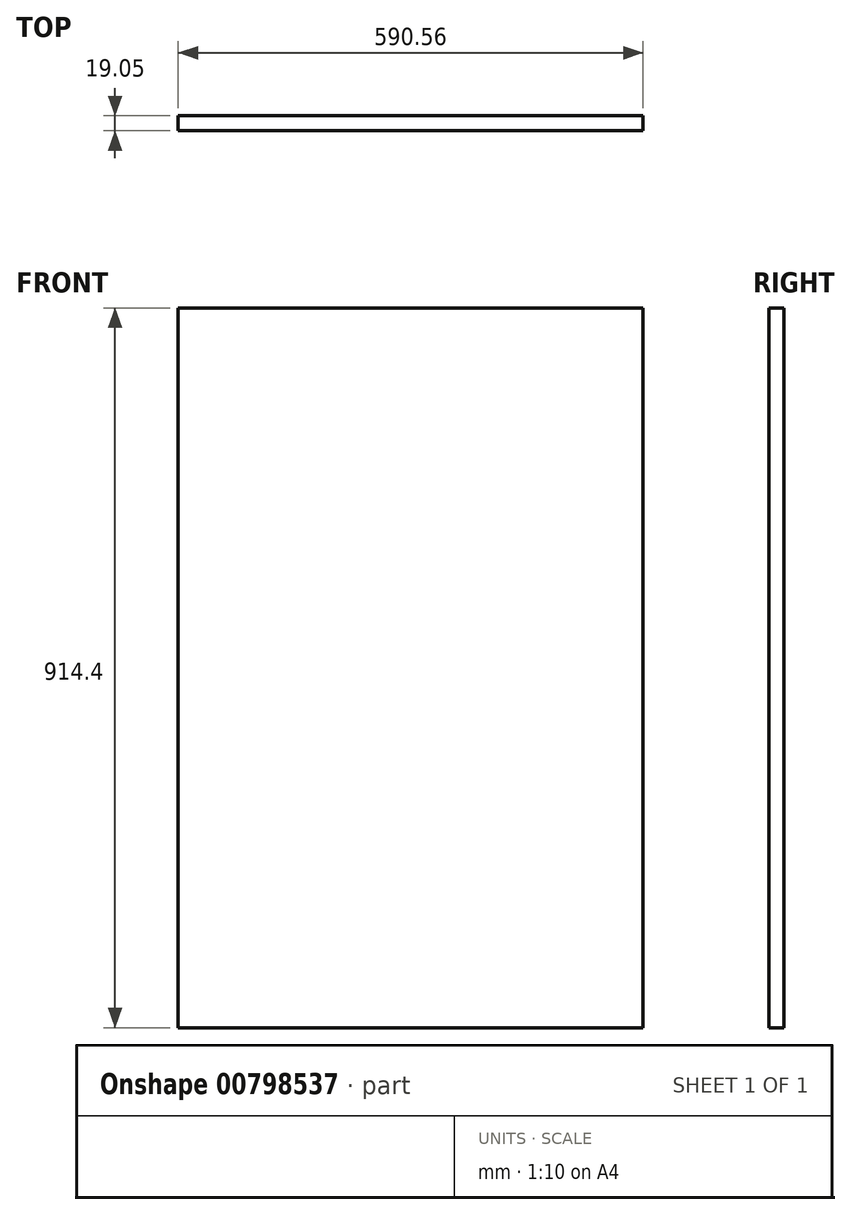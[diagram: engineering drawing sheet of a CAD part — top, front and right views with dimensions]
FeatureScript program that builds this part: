
annotation { "Feature Type Name" : "Feature", "Feature Type Description" : "" }
export const myFeature = defineFeature(function(context is Context, id is Id, definition is map)
    precondition{}
    {
        {
            var Q0;
            Q0=qCreatedBy(makeId("Front.planeOp"),FACE);
            var sketch = newSketch(context, id + "F0", { "sketchPlane" : qUnion([Q0])});
            skLineSegment(sketch, "E0.bottom", {"start": v(295.28, 457.2) * mm, "end": v(-295.28, 457.2) * mm});
            skLineSegment(sketch, "E0.top", {"start": v(295.28, -457.2) * mm, "end": v(-295.28, -457.2) * mm});
            skLineSegment(sketch, "E0.left", {"start": v(295.28, 457.2) * mm, "end": v(295.28, -457.2) * mm});
            skLineSegment(sketch, "E0.right", {"start": v(-295.28, 457.2) * mm, "end": v(-295.28, -457.2) * mm});
            skPoint(sketch, "E0.middle", {"position": v(0, 0) * mm});
            skSolve(sketch);
        }
        {
            var Q0;
            Q0 = qSketchRegion(id + "F0", true);
            extrude(context, id + "F1", {"entities" : qUnion([Q0]), "depth" : 19.05 * mm, "offsetDistance" : 30.48 * mm});
        }
    });
